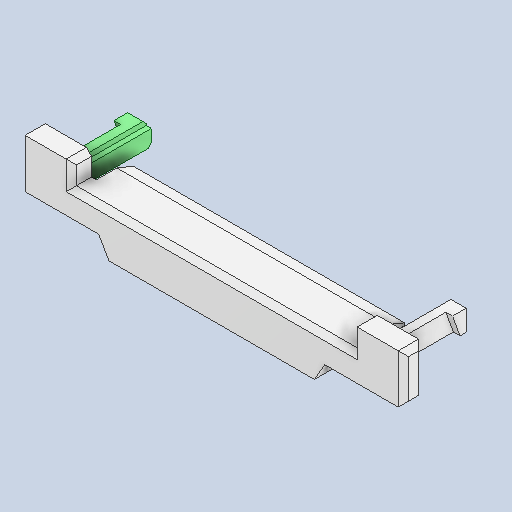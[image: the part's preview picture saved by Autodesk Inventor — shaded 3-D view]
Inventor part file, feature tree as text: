
AUTODESK INVENTOR PART (.ipt)
format: ipt  version: 2022 (Build 260153000, 153)  size: 126,976 bytes
history: mixed  units: in
note: dims shown in document units (in); Inventor stores cm internally (conversion verified against a paired STEP export)
features: chamfer x1, other x1, mirror x1, imported_body x1
ambient origin geometry x8: Origin, YZ Plane, XZ Plane, XY Plane, X Axis, Y Axis, Z Axis, Center Point
bodies: Solid1 (imported_parasolid), Solid2 (imported_parasolid), Solid3 (imported_parasolid)
feature tree (4):
  chamfer  "Chamfer2"  [1 undecoded]
  other  "Cut-Extrude3"
  mirror  "Mirror1"
  imported_body  NMx_Import_Brep_tag  [imported B-rep: ~58 faces, bbox_mm=[22.4, 3.9, 5.18]]
note: 1 required parameter value undecoded (feature->parameter linkage not recoverable at this tier; creation-order binding heuristic only, values carry confidence <= 0.55)
